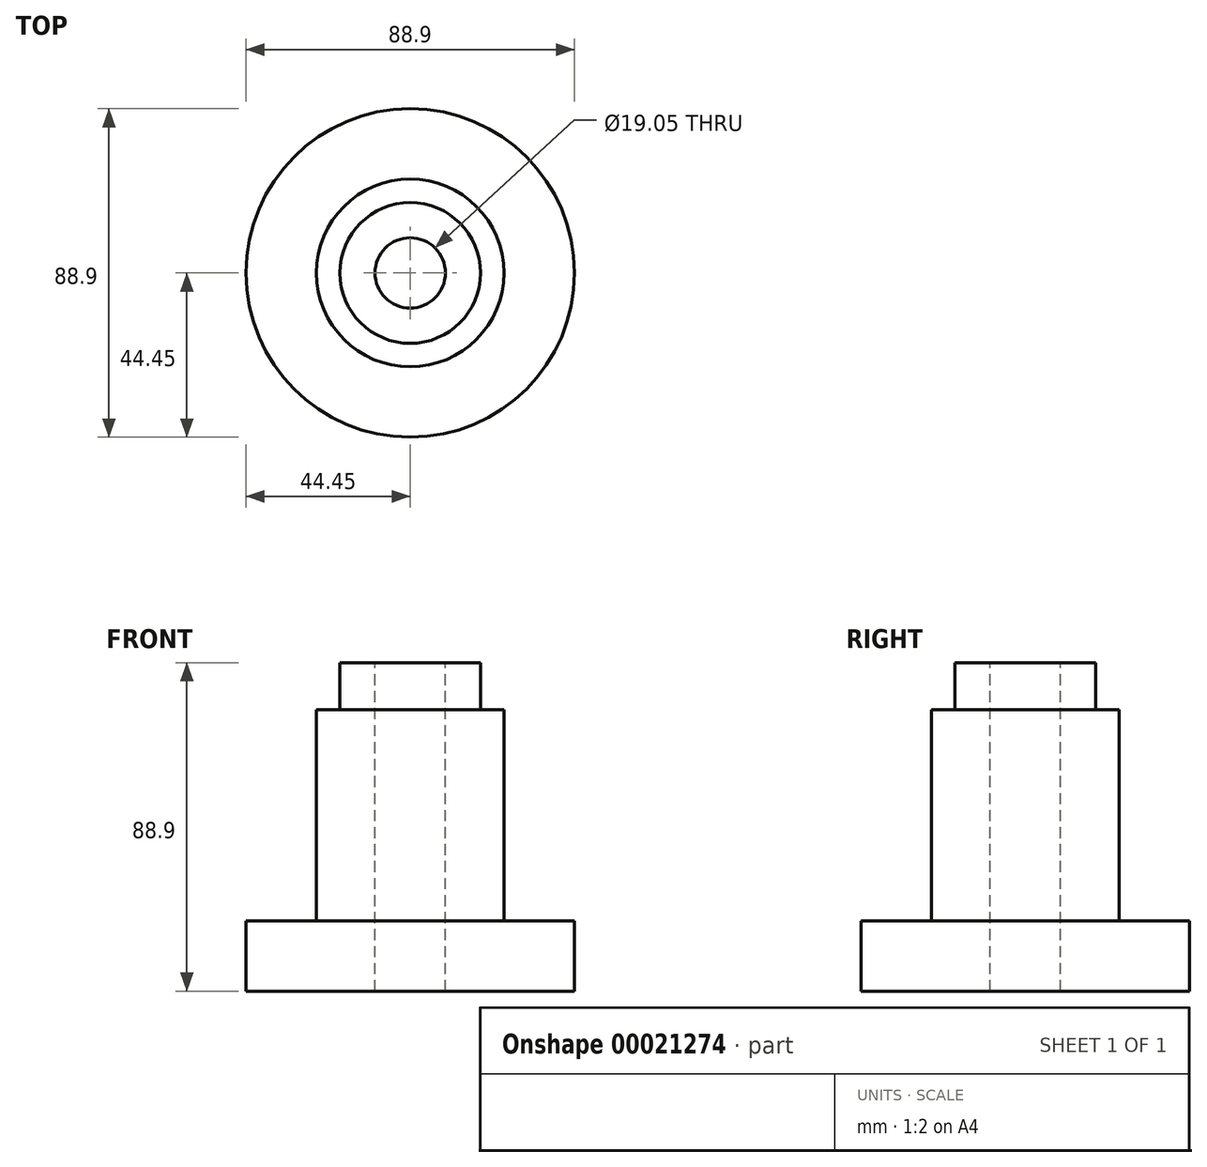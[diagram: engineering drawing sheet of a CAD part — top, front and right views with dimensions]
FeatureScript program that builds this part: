
annotation { "Feature Type Name" : "Feature", "Feature Type Description" : "" }
export const myFeature = defineFeature(function(context is Context, id is Id, definition is map)
    precondition{}
    {
        {
            var Q0;
            Q0=qCreatedBy(makeId("Top.planeOp"),FACE);
            var sketch = newSketch(context, id + "F0", { "sketchPlane" : qUnion([Q0])});
            skCircle(sketch, "E0", {"center": v(0, 0) * mm, "radius": 44.45 * mm});
            skSolve(sketch);
        }
        {
            var Q0;
            Q0=makeQuery(id+"F0.imprint","IMPRINT",FACE,{"disambiguationData":[TD([[makeQuery(id+"F0.imprint","IMPRINT",EDGE,{"derivedFrom":sQuery(id+"F0.wireOp",EDGE,"E0")}),1.0]])]});
            extrude(context, id + "F1", {"entities" : qUnion([Q0]), "depth" : 19.05 * mm});
        }
        {
            var Q0;
            Q0=makeQuery(id+"F1.opExtrude","CAP_FACE",FACE,{"disambiguationData":[OSD([sQuery(id+"F0.wireOp",EDGE,"E0")])],"isStart":false});
            var sketch = newSketch(context, id + "F2", { "sketchPlane" : qUnion([Q0])});
            skCircle(sketch, "E1", {"center": v(0, 0) * mm, "radius": 25.4 * mm});
            skSolve(sketch);
        }
        {
            var Q0;
            Q0=makeQuery(id+"F2.imprint","IMPRINT",FACE,{"disambiguationData":[TD([[makeQuery(id+"F2.imprint","IMPRINT",EDGE,{"derivedFrom":sQuery(id+"F2.wireOp",EDGE,"E1")}),1.0]])]});
            extrude(context, id + "F3", {"entities" : qUnion([Q0]), "operationType" : NewBodyOperationType.ADD, "depth" : 57.15 * mm});
        }
        {
            var Q0;
            Q0=makeQuery(id+"F3.opExtrude","CAP_FACE",FACE,{"disambiguationData":[OSD([sQuery(id+"F2.wireOp",EDGE,"E1")])],"isStart":false});
            var sketch = newSketch(context, id + "F4", { "sketchPlane" : qUnion([Q0])});
            skCircle(sketch, "E2", {"center": v(0, 0) * mm, "radius": 19.05 * mm});
            skSolve(sketch);
        }
        {
            var Q0;
            Q0=makeQuery(id+"F4.imprint","IMPRINT",FACE,{"disambiguationData":[TD([[makeQuery(id+"F4.imprint","IMPRINT",EDGE,{"derivedFrom":sQuery(id+"F4.wireOp",EDGE,"E2")}),1.0]])]});
            extrude(context, id + "F5", {"entities" : qUnion([Q0]), "operationType" : NewBodyOperationType.ADD, "depth" : 12.7 * mm});
        }
        {
            var Q0;
            Q0=makeQuery(id+"F5.opExtrude","CAP_FACE",FACE,{"disambiguationData":[OSD([sQuery(id+"F4.wireOp",EDGE,"E2")])],"isStart":false});
            var sketch = newSketch(context, id + "F6", { "sketchPlane" : qUnion([Q0])});
            skCircle(sketch, "E3", {"center": v(0, 0) * mm, "radius": 9.53 * mm});
            skSolve(sketch);
        }
        {
            var Q0;
            Q0=makeQuery(id+"F6.imprint","IMPRINT",FACE,{"disambiguationData":[TD([[makeQuery(id+"F6.imprint","IMPRINT",EDGE,{"derivedFrom":sQuery(id+"F6.wireOp",EDGE,"E3")}),1.0]])]});
            extrude(context, id + "F7", {"entities" : qUnion([Q0]), "operationType" : NewBodyOperationType.REMOVE, "oppositeDirection" : true, "depth" : 88.9 * mm});
        }
    });
